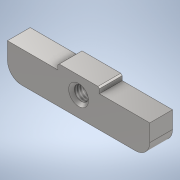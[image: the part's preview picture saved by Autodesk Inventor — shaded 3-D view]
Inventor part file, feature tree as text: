
AUTODESK INVENTOR PART (.ipt)
format: ipt  version: 2020 (Build 240168000, 168)  size: 194,048 bytes
history: native  units: mm
features: other x2, extrude x1, chamfer x1
ambient origin geometry x8: Origin, YZ Plane, XZ Plane, XY Plane, X Axis, Y Axis, Z Axis, Center Point
bodies: Body1 (feature_tree)
feature tree (4):
  other  "實體1"
  extrude  "擠出1"  Depth=50.0mm
  other  "螺紋1"
  chamfer  "倒角1"  Distance=8.0mm
